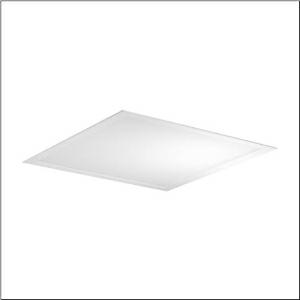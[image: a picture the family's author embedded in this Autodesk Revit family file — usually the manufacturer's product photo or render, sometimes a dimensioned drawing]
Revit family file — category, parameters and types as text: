
# Revit family: apollon_r__31_square_51mp11wd2442_8a23
name_source: partatom
category: Lighting Fixtures
units: mm (PartAtom-declared; Revit-internal decimal feet)

## family parameters
Cut with Voids When Loaded = No
Host = Face
Light Source = No
Part Type = Normal
Room Calculation Point = No
Round Connector Dimension = Use Diameter
Shared = No

## types (1)
- Apollon® 31 square (1 x LED, 4000 lm, 27.5 W, 4000K)
    Apparent Load = 28 VA
    CIE Flux Codes = 61 87 97 100 100
    Color Rendering = 80
    Color Temperature = 4000K
    Default Elevation = 1800 mm
    Description = Apollon® 31 square, office luminaire, primary optical cover: micro prismatic cover, of PMMA, CAT 2 (L<= 3000cd/m²), light emission: direct distribution, primary light characteristic: symmetric, installation type: lay-in mounting, LED, rated luminous flux: 4.000lm, luminous efficacy: 145lm/W, light colour: 840, colour temperature: 4000K, control gear: DALI 2, Multilumen, with terminal, 5-pole, mains connection: 220..240V, AC/DC, 0/50..60Hz, rated input power: 28W, housing, of aluminium, traffic white (RAL 9016), module: M625, length: 620mm, width: 620mm, height: 62mm, recess depth: 180mm, housing upper side, of sheet steel, coated, protection rating (complete): IP20, protection rating (on room side): IP40, insulation class (complete): insulation class II (safety insulation), certification: CE, ENEC, impact resistance: IK03, permissible operating ambient temperature: -20..+40°C, permissible storage temperature: -20..+60°C, standard: EN 60598-2-22, packaging unit: 1 piece
    Height = 0 mm  [stored 0 ft]
    Lamp = 1 x LED
    Lamp Light Flux = 4000 lm
    Lamp Power = 27.5 W
    Lamp count = 1
    Length = 620 mm
    Luminous efficacy = 145 lm/W
    Manufacturer = Siteco
    ModVariant = No
    Model = 51MP11WD2442
    Mounting Place = Ceiling
    Mounting Type = Recessed
    Number of Poles = 1
    OnlyDefault = Yes
    Power Factor = 1
    Product Name = Apollon® 31 square
    Product group = office luminaire | ceiling recessed
    ProductGroupID = 401
    Protection Class = Protection class II
    Protection Degree = IP 20
    RLX_Detail_Level = 1
    RLX_Emergency_Light_Flux = 0 lm
    RLX_Emergency_Type = 0
    RLX_Emergency_Type_DB = No
    RlxData = <blob elided: 13025 chars, md5=c7c798bd>
    Socket = socket
    Standby Power = 0 W
    System Light Flux = 4000 lm
    System Power = 28 W
    Type Comments = Product without accessories
    Type Image = l_1291039.jpg
    URL = http://relux.com
    VarID = ---
    Voltage = 0 V
    Weight = 0.00 kg
    Width = 620 mm

note: [stored X ft] marks values corroborated as IEEE doubles in the binary element streams (Revit-internal decimal feet)

## geometry (parser evidence)
native form markers: Sweep x10
no freeform markers — native parametric forms only
